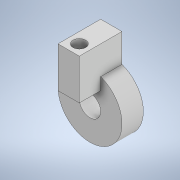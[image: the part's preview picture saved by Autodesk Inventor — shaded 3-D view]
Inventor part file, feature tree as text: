
AUTODESK INVENTOR PART (.ipt)
format: ipt  version: 2022 (Build 260153000, 153)  size: 128,000 bytes
history: native  units: in
note: dims shown in document units (in); Inventor stores cm internally (conversion verified against a paired STEP export)
features: extrude x3, sketch x3
ambient origin geometry x8: Origin, YZ Plane, XZ Plane, XY Plane, X Axis, Y Axis, Z Axis, Center Point
bodies: Solid1 (feature_tree)
feature tree (6):
  extrude  "Extrusion1"  Depth=0.7874in
  extrude  "Extrusion2"  Depth=0.7874in
  extrude  "Extrusion3"  Depth=1.5748in TaperAngle=0.0deg
  sketch  "Sketch1"  dims[d0=2.3622in d1=0.7874in]
  sketch  "Sketch2"  dims[d2=0.7874in d3=0.7874in]
  sketch  "Sketch3"  dims[d4=1.378in d5=1.5748in d6=0.0in d7=1.4961in d8=0.7874in d9=0.0in d10=0.4724in d11=1.5876in d12=0.0in]
